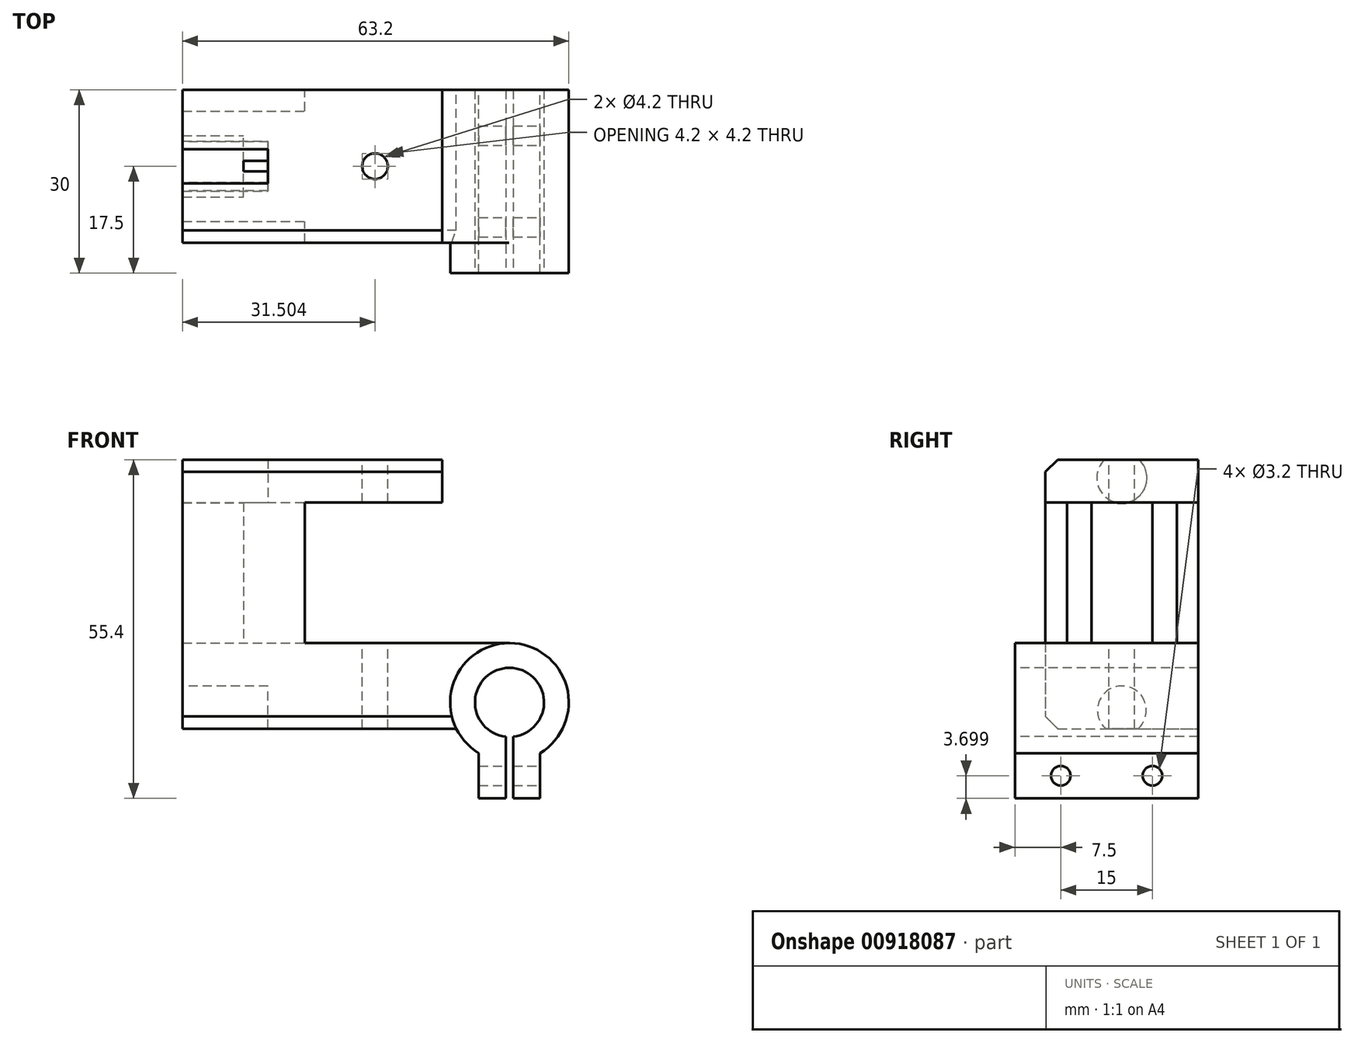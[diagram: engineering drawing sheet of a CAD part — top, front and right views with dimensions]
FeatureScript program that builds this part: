
annotation { "Feature Type Name" : "Feature", "Feature Type Description" : "" }
export const myFeature = defineFeature(function(context is Context, id is Id, definition is map)
    precondition{}
    {
        {
            var Q0;
            Q0=qCreatedBy(makeId("Front.planeOp"),FACE);
            var sketch = newSketch(context, id + "F0", { "sketchPlane" : qUnion([Q0])});
            skLineSegment(sketch, "E0", {"start": v(-4.59, -4.3) * mm, "end": v(30.22, -4.3) * mm});
            skLineSegment(sketch, "E1", {"start": v(38.98, 9.7) * mm, "end": v(-4.59, 9.7) * mm});
            skLineSegment(sketch, "E2", {"start": v(-4.59, 39.7) * mm, "end": v(-14.59, 39.7) * mm});
            skLineSegment(sketch, "E3", {"start": v(-14.59, 39.7) * mm, "end": v(-14.59, -4.3) * mm});
            skLineSegment(sketch, "E4", {"start": v(-14.59, -4.3) * mm, "end": v(-4.59, -4.3) * mm});
            skLineSegment(sketch, "E5", {"start": v(-4.59, 39.7) * mm, "end": v(20.41, 39.7) * mm});
            skLineSegment(sketch, "E6", {"start": v(20.41, 39.7) * mm, "end": v(20.41, 32.7) * mm});
            skLineSegment(sketch, "E7", {"start": v(20.41, 32.7) * mm, "end": v(-4.59, 32.7) * mm});
            skLineSegment(sketch, "E8", {"start": v(-4.59, 32.7) * mm, "end": v(-4.59, 9.7) * mm});
            skArc(sketch, "E9", {"start": v(38.93, -5.6) * mm, "mid": v(38.91, 5.6) * mm, "end": v(38.9, -5.6) * mm});
            skArc(sketch, "E10", {"start": v(43.93, -8.3) * mm, "mid": v(38.91, 9.7) * mm, "end": v(33.9, -8.3) * mm});
            skLineSegment(sketch, "E11", {"start": v(38.9, -5.6) * mm, "end": v(38.9, -9.7) * mm});
            skLineSegment(sketch, "E12", {"start": v(38.93, -5.6) * mm, "end": v(38.93, -9.7) * mm});
            skLineSegment(sketch, "E13", {"start": v(38.9, -9.7) * mm, "end": v(38.9, -15.7) * mm});
            skLineSegment(sketch, "E14", {"start": v(38.93, -9.7) * mm, "end": v(38.93, -15.7) * mm});
            skLineSegment(sketch, "E15", {"start": v(38.9, -15.7) * mm, "end": v(33.9, -15.7) * mm});
            skLineSegment(sketch, "E16", {"start": v(38.93, -15.7) * mm, "end": v(43.93, -15.7) * mm});
            skLineSegment(sketch, "E17", {"start": v(33.9, -15.7) * mm, "end": v(33.9, -8.3) * mm});
            skLineSegment(sketch, "E18", {"start": v(43.93, -15.7) * mm, "end": v(43.93, -8.3) * mm});
            skSolve(sketch);
        }
        {
            var Q0;
            Q0=makeQuery(id+"F0.imprint","IMPRINT",FACE,{"disambiguationData":[TD([[makeQuery(id+"F0.imprint","IMPRINT",EDGE,{"derivedFrom":sQuery(id+"F0.wireOp",EDGE,"E0")}),1.0]])]});
            extrude(context, id + "F1", {"entities" : qUnion([Q0]), "depth" : 25 * mm});
        }
        {
            var Q0;
            Q0=makeQuery(id+"F1.opExtrude","SWEPT_FACE",FACE,{"disambiguationData":[OSD([sQuery(id+"F0.wireOp",EDGE,"E3")])]});
            var sketch = newSketch(context, id + "F2", { "sketchPlane" : qUnion([Q0])});
            skLineSegment(sketch, "E19", {"start": v(12.5, 39.7) * mm, "end": v(12.5, -4.3) * mm, "construction": true});
            skCircle(sketch, "E20", {"center": v(12.5, 36.7) * mm, "radius": 4 * mm});
            skCircle(sketch, "E21", {"center": v(12.5, -1.31) * mm, "radius": 4 * mm});
            skCircle(sketch, "E22", {"center": v(24, 33.55) * mm, "radius": 1.75 * mm});
            skCircle(sketch, "E23", {"center": v(24, 1.85) * mm, "radius": 1.75 * mm});
            skLineSegment(sketch, "E24", {"start": v(24, 31.8) * mm, "end": v(25, 31.8) * mm});
            skLineSegment(sketch, "E25", {"start": v(25, 35.3) * mm, "end": v(24, 35.3) * mm});
            skLineSegment(sketch, "E26", {"start": v(24, 3.6) * mm, "end": v(25, 3.6) * mm});
            skLineSegment(sketch, "E27", {"start": v(24, 0.1) * mm, "end": v(25, 0.1) * mm});
            skSolve(sketch);
        }
        {
            var Q0;
            {var subQ0=makeQuery(id+"F1.opExtrude","SWEPT_EDGE",EDGE,{"disambiguationData":[OSD([sQuery(id+"F0.wireOp",EDGE,"E3"),sQuery(id+"F0.wireOp",EDGE,"E4")])]});var subQ1=sQuery(id+"F2.wireOp",EDGE,"E21");var subQ3=makeQuery(id+"F2.imprint","INTERSECT",VERTEX,{"disambiguationData":[OD(0.0)],"derivedFrom":[subQ0,subQ1]});Q0=makeQuery(id+"F2.imprint","IMPRINT",FACE,{"disambiguationData":[TD([[makeQuery(id+"F2.imprint","IMPRINT",EDGE,{"disambiguationData":[TD([[subQ3,-1.0]])],"derivedFrom":subQ1}),1.0]])]});}
            var Q1;
            {var subQ0=makeQuery(id+"F1.opExtrude","SWEPT_EDGE",EDGE,{"disambiguationData":[OSD([sQuery(id+"F0.wireOp",EDGE,"E3"),sQuery(id+"F0.wireOp",EDGE,"E4")])]});var subQ1=sQuery(id+"F2.wireOp",EDGE,"E21");var subQ3=makeQuery(id+"F2.imprint","INTERSECT",VERTEX,{"disambiguationData":[OD(0.0)],"derivedFrom":[subQ0,subQ1]});Q1=makeQuery(id+"F2.imprint","IMPRINT",FACE,{"disambiguationData":[TD([[makeQuery(id+"F2.imprint","IMPRINT",EDGE,{"disambiguationData":[TD([[subQ3,1.0]])],"derivedFrom":subQ1}),1.0]])]});}
            var Q2;
            {var subQ0=makeQuery(id+"F1.opExtrude","SWEPT_EDGE",EDGE,{"disambiguationData":[OSD([sQuery(id+"F0.wireOp",EDGE,"E2"),sQuery(id+"F0.wireOp",EDGE,"E3")])]});var subQ1=sQuery(id+"F2.wireOp",EDGE,"E20");var subQ3=makeQuery(id+"F2.imprint","INTERSECT",VERTEX,{"disambiguationData":[OD(0.0)],"derivedFrom":[subQ0,subQ1]});Q2=makeQuery(id+"F2.imprint","IMPRINT",FACE,{"disambiguationData":[TD([[makeQuery(id+"F2.imprint","IMPRINT",EDGE,{"disambiguationData":[TD([[subQ3,-1.0]])],"derivedFrom":subQ1}),1.0]])]});}
            var Q3;
            {var subQ0=makeQuery(id+"F1.opExtrude","SWEPT_EDGE",EDGE,{"disambiguationData":[OSD([sQuery(id+"F0.wireOp",EDGE,"E2"),sQuery(id+"F0.wireOp",EDGE,"E3")])]});var subQ1=sQuery(id+"F2.wireOp",EDGE,"E20");var subQ3=makeQuery(id+"F2.imprint","INTERSECT",VERTEX,{"disambiguationData":[OD(0.0)],"derivedFrom":[subQ0,subQ1]});Q3=makeQuery(id+"F2.imprint","IMPRINT",FACE,{"disambiguationData":[TD([[makeQuery(id+"F2.imprint","IMPRINT",EDGE,{"disambiguationData":[TD([[subQ3,1.0]])],"derivedFrom":subQ1}),1.0]])]});}
            extrude(context, id + "F3", {"entities" : qUnion([Q0, Q1, Q2, Q3]), "operationType" : NewBodyOperationType.REMOVE, "oppositeDirection" : true, "depth" : 14 * mm});
        }
        {
            var Q0;
            {var subQ1=sQuery(id+"F0.wireOp",EDGE,"E9");var subQ5=sQuery(id+"F0.wireOp",EDGE,"ac4ea8cb-b610-4921-a804-ed47c2f5f987");var subQ6=makeQuery(id+"F0.imprint","INTERSECT",VERTEX,{"derivedFrom":[subQ1,subQ5]});Q0=makeQuery(id+"F0.imprint","IMPRINT",FACE,{"disambiguationData":[TD([[makeQuery(id+"F0.imprint","IMPRINT",EDGE,{"disambiguationData":[TD([[subQ6,-1.0]])],"derivedFrom":subQ1}),-1.0]])]});}
            var Q1;
            {var subQ1=sQuery(id+"F0.wireOp",EDGE,"e6592883-06e4-4a0a-b0ea-33459a304d32");Q1=makeQuery(id+"F0.imprint","IMPRINT",FACE,{"disambiguationData":[TD([[makeQuery(id+"F0.imprint","IMPRINT",EDGE,{"derivedFrom":subQ1}),1.0]])]});}
            var Q2;
            {var subQ0=sQuery(id+"F0.wireOp",EDGE,"b1df3230-600c-49be-9040-62ce0c415bc6");Q2=makeQuery(id+"F0.imprint","IMPRINT",FACE,{"disambiguationData":[TD([[makeQuery(id+"F0.imprint","IMPRINT",EDGE,{"derivedFrom":subQ0}),-1.0]])]});}
            extrude(context, id + "F4", {"entities" : qUnion([Q0, Q1, Q2]), "operationType" : NewBodyOperationType.ADD, "depth" : 30 * mm});
        }
        {
            var Q0;
            Q0=makeQuery(id+"F1.opExtrude","CAP_EDGE",EDGE,{"disambiguationData":[OSD([sQuery(id+"F0.wireOp",EDGE,"E4")])],"isStart":false});
            var Q1;
            Q1=makeQuery(id+"F1.opExtrude","CAP_EDGE",EDGE,{"disambiguationData":[OSD([sQuery(id+"F0.wireOp",EDGE,"E2")])],"isStart":false});
            chamfer(context, id + "F5", {"entities" : qUnion([Q0, Q1]), "width" : 2 * mm, "tangentPropagation" : true});
        }
        {
            var Q0;
            Q0=makeQuery(id+"F4.opExtrude","SWEPT_FACE",FACE,{"disambiguationData":[OSD([sQuery(id+"F0.wireOp",EDGE,"E18")])]});
            var sketch = newSketch(context, id + "F6", { "sketchPlane" : qUnion([Q0])});
            skLineSegment(sketch, "E28", {"start": v(-15, -8.3) * mm, "end": v(-30, -8.3) * mm});
            skLineSegment(sketch, "E29", {"start": v(-22.5, -8.3) * mm, "end": v(-22.5, -15.7) * mm});
            skLineSegment(sketch, "E30", {"start": v(-15, -8.3) * mm, "end": v(0, -8.3) * mm});
            skLineSegment(sketch, "E31", {"start": v(-7.5, -8.3) * mm, "end": v(-7.5, -15.7) * mm});
            skCircle(sketch, "E32", {"center": v(-22.5, -12) * mm, "radius": 1.6 * mm});
            skCircle(sketch, "E33", {"center": v(-7.5, -12) * mm, "radius": 1.6 * mm});
            skSolve(sketch);
        }
        {
            var Q0;
            Q0=qSketchRegion(id+"F6",true);
            extrude(context, id + "F7", {"entities" : qUnion([Q0]), "operationType" : NewBodyOperationType.REMOVE, "oppositeDirection" : true, "depth" : 25 * mm});
        }
        {
            var Q0;
            Q0=makeQuery(id+"F1.opExtrude","SWEPT_FACE",FACE,{"disambiguationData":[OSD([sQuery(id+"F0.wireOp",EDGE,"E8")])]});
            var sketch = newSketch(context, id + "F8", { "sketchPlane" : qUnion([Q0])});
            skLineSegment(sketch, "E34", {"start": v(-12.5, 32.7) * mm, "end": v(-12.5, 9.7) * mm});
            skLineSegment(sketch, "E35", {"start": v(-21.5, 22.93) * mm, "end": v(-21.5, 32.7) * mm});
            skLineSegment(sketch, "E36", {"start": v(-21.5, 32.7) * mm, "end": v(-25, 32.7) * mm});
            skLineSegment(sketch, "E37", {"start": v(-25, 32.7) * mm, "end": v(-25, 9.7) * mm});
            skLineSegment(sketch, "E38", {"start": v(-25, 9.7) * mm, "end": v(-21.5, 9.7) * mm});
            skLineSegment(sketch, "E39", {"start": v(-21.5, 9.7) * mm, "end": v(-21.5, 22.93) * mm});
            skLineSegment(sketch, "E40", {"start": v(-3.5, 21.2) * mm, "end": v(-3.5, 32.7) * mm});
            skLineSegment(sketch, "E41", {"start": v(-3.5, 21.2) * mm, "end": v(-3.5, 9.7) * mm});
            skLineSegment(sketch, "E42", {"start": v(-3.5, 9.7) * mm, "end": v(0, 9.7) * mm});
            skLineSegment(sketch, "E43", {"start": v(0, 9.7) * mm, "end": v(0, 32.7) * mm});
            skLineSegment(sketch, "E44", {"start": v(0, 32.7) * mm, "end": v(-3.5, 32.7) * mm});
            skLineSegment(sketch, "E45", {"start": v(-12.5, 32.7) * mm, "end": v(-7.5, 32.7) * mm});
            skLineSegment(sketch, "E46", {"start": v(-12.5, 32.7) * mm, "end": v(-17.5, 32.7) * mm});
            skLineSegment(sketch, "E47", {"start": v(-17.5, 32.7) * mm, "end": v(-17.5, 9.7) * mm});
            skLineSegment(sketch, "E48", {"start": v(-7.5, 32.7) * mm, "end": v(-7.5, 9.7) * mm});
            skLineSegment(sketch, "E49", {"start": v(-7.5, 9.7) * mm, "end": v(-17.5, 9.7) * mm});
            skLineSegment(sketch, "E50", {"start": v(-21.5, 32.7) * mm, "end": v(-17.5, 32.7) * mm});
            skLineSegment(sketch, "E51", {"start": v(-7.5, 32.7) * mm, "end": v(-3.5, 32.7) * mm});
            skLineSegment(sketch, "E52", {"start": v(-7.5, 9.7) * mm, "end": v(-3.5, 9.7) * mm});
            skLineSegment(sketch, "E53", {"start": v(-17.5, 9.7) * mm, "end": v(-21.5, 9.7) * mm});
            skSolve(sketch);
        }
        {
            var Q0;
            Q0=makeQuery(id+"F8.imprint","IMPRINT",FACE,{"disambiguationData":[TD([[makeQuery(id+"F8.imprint","IMPRINT",EDGE,{"derivedFrom":sQuery(id+"F8.wireOp",EDGE,"E35")}),-1.0]])]});
            var Q1;
            Q1=makeQuery(id+"F8.imprint","IMPRINT",FACE,{"disambiguationData":[TD([[makeQuery(id+"F8.imprint","IMPRINT",EDGE,{"derivedFrom":sQuery(id+"F8.wireOp",EDGE,"E40")}),1.0]])]});
            extrude(context, id + "F9", {"entities" : qUnion([Q0, Q1]), "operationType" : NewBodyOperationType.REMOVE, "oppositeDirection" : true, "depth" : 25 * mm});
        }
        {
            var Q0;
            {var subQ0=sQuery(id+"F0.wireOp",EDGE,"E1");Q0=makeQuery(id+"F9.boolean.opBoolean","MERGE",FACE,{"derivedFrom":[makeQuery(id+"F4.boolean.opBoolean","MERGE",FACE,{"derivedFrom":[makeQuery(id+"F1.opExtrude","SWEPT_FACE",FACE,{"disambiguationData":[OSD([subQ0])]}),makeQuery(id+"F4.opExtrude","SWEPT_FACE",FACE,{"disambiguationData":[OSD([subQ0])]})]}),makeQuery(id+"F9.opExtrude","SWEPT_FACE",FACE,{"disambiguationData":[OSD([sQuery(id+"F8.wireOp",EDGE,"E52")])]}),makeQuery(id+"F9.opExtrude","SWEPT_FACE",FACE,{"disambiguationData":[OSD([sQuery(id+"F8.wireOp",EDGE,"E53")])]})]});}
            var sketch = newSketch(context, id + "F10", { "sketchPlane" : qUnion([Q0])});
            skCircle(sketch, "E54", {"center": v(11.41, -12.5) * mm, "radius": 15 * mm});
            skPoint(sketch, "E55", {"position": v(26.41, -12.5) * mm});
            skLineSegment(sketch, "E56", {"start": v(26.41, -12.5) * mm, "end": v(16.91, -12.5) * mm});
            skCircle(sketch, "E57", {"center": v(16.91, -12.5) * mm, "radius": 6.34 * mm});
            skCircle(sketch, "E58", {"center": v(16.91, -12.5) * mm, "radius": 8 * mm});
            skCircle(sketch, "E59", {"center": v(16.91, -12.5) * mm, "radius": 2.1 * mm});
            skSolve(sketch);
        }
        {
            var Q0;
            {var subQ2=sQuery(id+"F0.wireOp",EDGE,"E8");Q0=makeQuery(id+"F9.boolean.opBoolean","SPLIT",FACE,{"disambiguationData":[TD([makeQuery(id+"F9.opExtrude","SWEPT_FACE",FACE,{"disambiguationData":[OSD([sQuery(id+"F8.wireOp",EDGE,"E35"),sQuery(id+"F8.wireOp",EDGE,"E39")])]})])],"derivedFrom":makeQuery(id+"F1.opExtrude","SWEPT_FACE",FACE,{"disambiguationData":[OSD([subQ2])]})});}
            var Q1;
            {var subQ3=sQuery(id+"F0.wireOp",EDGE,"E8");Q1=makeQuery(id+"F9.boolean.opBoolean","SPLIT",FACE,{"disambiguationData":[TD([makeQuery(id+"F9.opExtrude","SWEPT_FACE",FACE,{"disambiguationData":[OSD([sQuery(id+"F8.wireOp",EDGE,"E40"),sQuery(id+"F8.wireOp",EDGE,"E41")])]})])],"derivedFrom":makeQuery(id+"F1.opExtrude","SWEPT_FACE",FACE,{"disambiguationData":[OSD([subQ3])]})});}
            extrude(context, id + "F11", {"entities" : qUnion([Q0, Q1]), "operationType" : NewBodyOperationType.ADD, "depth" : 10 * mm});
        }
        {
            var Q0;
            Q0=makeQuery(id+"F10.imprint","IMPRINT",FACE,{"disambiguationData":[TD([[makeQuery(id+"F10.imprint","IMPRINT",EDGE,{"derivedFrom":sQuery(id+"F10.wireOp",EDGE,"E59")}),1.0]])]});
            extrude(context, id + "F12", {"entities" : qUnion([Q0]), "operationType" : NewBodyOperationType.REMOVE, "oppositeDirection" : true, "depth" : 50 * mm, "hasSecondDirection" : true, "secondDirectionOppositeDirection" : false, "secondDirectionDepth" : 50 * mm});
        }
        {
            var Q0;
            Q0=makeQuery(id+"F1.opExtrude","SWEPT_FACE",FACE,{"disambiguationData":[OSD([sQuery(id+"F0.wireOp",EDGE,"E6")])]});
            var sketch = newSketch(context, id + "F13", { "sketchPlane" : qUnion([Q0])});
            skLineSegment(sketch, "E60", {"start": v(-23, 39.7) * mm, "end": v(-25, 37.7) * mm});
            skLineSegment(sketch, "E61", {"start": v(-25, 37.7) * mm, "end": v(-25, 32.7) * mm});
            skLineSegment(sketch, "E62", {"start": v(-25, 32.7) * mm, "end": v(0, 32.7) * mm});
            skLineSegment(sketch, "E63", {"start": v(0, 32.7) * mm, "end": v(0, 39.7) * mm});
            skLineSegment(sketch, "E64", {"start": v(0, 39.7) * mm, "end": v(-23, 39.7) * mm});
            skSolve(sketch);
        }
        {
            var Q0;
            Q0=qSketchRegion(id+"F13",true);
            extrude(context, id + "F14", {"entities" : qUnion([Q0]), "operationType" : NewBodyOperationType.ADD, "depth" : 7.5 * mm});
        }
        {
            var Q0;
            Q0=makeQuery(id+"F4.opExtrude","CAP_FACE",FACE,{"disambiguationData":[OSD([sQuery(id+"F0.wireOp",EDGE,"E1"),sQuery(id+"F0.wireOp",EDGE,"E9"),sQuery(id+"F0.wireOp",EDGE,"E10"),sQuery(id+"F0.wireOp",EDGE,"E11"),sQuery(id+"F0.wireOp",EDGE,"E12"),sQuery(id+"F0.wireOp",EDGE,"E13"),sQuery(id+"F0.wireOp",EDGE,"E14"),sQuery(id+"F0.wireOp",EDGE,"E15"),sQuery(id+"F0.wireOp",EDGE,"E16"),sQuery(id+"F0.wireOp",EDGE,"E17"),sQuery(id+"F0.wireOp",EDGE,"E18")])],"isStart":false});
            var sketch = newSketch(context, id + "F15", { "sketchPlane" : qUnion([Q0])});
            skArc(sketch, "E65", {"start": v(39.53, -5.62) * mm, "mid": v(38.9, 5.65) * mm, "end": v(38.31, -5.62) * mm});
            skLineSegment(sketch, "E66", {"start": v(38.91, 0) * mm, "end": v(38.91, -15.73) * mm});
            skLineSegment(sketch, "E67", {"start": v(38.91, -15.73) * mm, "end": v(38.93, -15.73) * mm});
            skLineSegment(sketch, "E68", {"start": v(38.93, -15.73) * mm, "end": v(38.93, -15.7) * mm});
            skLineSegment(sketch, "E69", {"start": v(38.93, -15.7) * mm, "end": v(38.91, -15.7) * mm});
            skLineSegment(sketch, "E70", {"start": v(38.91, -15.7) * mm, "end": v(38.31, -15.7) * mm});
            skLineSegment(sketch, "E71", {"start": v(38.93, -15.7) * mm, "end": v(39.53, -15.7) * mm});
            skLineSegment(sketch, "E72", {"start": v(39.53, -15.7) * mm, "end": v(39.53, -5.62) * mm});
            skLineSegment(sketch, "E73", {"start": v(38.31, -15.7) * mm, "end": v(38.31, -5.62) * mm});
            skSolve(sketch);
        }
        {
            var Q0;
            Q0=qSketchRegion(id+"F15",true);
            extrude(context, id + "F16", {"entities" : qUnion([Q0]), "operationType" : NewBodyOperationType.REMOVE, "oppositeDirection" : true, "depth" : 30 * mm});
        }
        {
            var Q0;
            Q0=makeQuery(id+"F3.boolean.opBoolean","COPY",FACE,{"derivedFrom":makeQuery(id+"F3.opExtrude","CAP_FACE",FACE,{"disambiguationData":[OSD([sQuery(id+"F2.wireOp",EDGE,"E20")])],"isStart":false})});
            var sketch = newSketch(context, id + "F17", { "sketchPlane" : qUnion([Q0])});
            skCircle(sketch, "E74", {"center": v(12.5, 36.7) * mm, "radius": 4.1 * mm});
            skSolve(sketch);
        }
        {
            var Q0;
            Q0=qSketchRegion(id+"F17",true);
            extrude(context, id + "F18", {"entities" : qUnion([Q0]), "operationType" : NewBodyOperationType.REMOVE, "depth" : 25 * mm});
        }
    });
